FCSTD DOCUMENT  (FreeCAD 1.0R38806 (Git))
Label: ex-005
License: All rights reserved
LicenseURL: https://en.wikipedia.org/wiki/All_rights_reserved
objects: TechDraw::DrawViewDimension×18, Sketcher::SketchObject×2, TechDraw::DrawSVGTemplate×1, TechDraw::DrawProjGroupItem×1, TechDraw::DrawPage×1
note: 24 computed .brp shape members not serialized (recipe doc carries the construction recipe); baked Part::Feature solids carry a one-line shape summary decoded from their .brp

FEATURE [Sketcher::SketchObject] Sketch
  ArcFitTolerance = 1e-06
  FullyConstrained = false
  MakeInternals = false
  sketch-geometry (36):
    g0: LineSegment StartX=0 StartY=0 StartZ=0 EndX=5 EndY=0 EndZ=0
    g1: LineSegment StartX=5 StartY=0 StartZ=0 EndX=5 EndY=2 EndZ=0
    g2: LineSegment StartX=5 StartY=2 StartZ=0 EndX=3 EndY=2 EndZ=0
    g3: LineSegment StartX=3 StartY=2 StartZ=0 EndX=3 EndY=6 EndZ=0
    g4: LineSegment StartX=3 StartY=6 StartZ=0 EndX=5 EndY=6 EndZ=0
    g5: LineSegment StartX=5 StartY=6 StartZ=0 EndX=5 EndY=8 EndZ=0
    g6: LineSegment StartX=5 StartY=8 StartZ=0 EndX=9 EndY=8 EndZ=0
    g7: LineSegment StartX=9 StartY=8 StartZ=0 EndX=9 EndY=12 EndZ=0
    g8: LineSegment StartX=9 StartY=12 StartZ=0 EndX=17 EndY=12 EndZ=0
    g9: LineSegment StartX=17 StartY=12 StartZ=0 EndX=17 EndY=8 EndZ=0
    g10: LineSegment StartX=17 StartY=8 StartZ=0 EndX=21 EndY=8 EndZ=0
    g11: LineSegment StartX=21 StartY=8 StartZ=0 EndX=21 EndY=6 EndZ=0
    g12: LineSegment StartX=21 StartY=6 StartZ=0 EndX=23 EndY=6 EndZ=0
    g13: LineSegment StartX=23 StartY=6 StartZ=0 EndX=23 EndY=2 EndZ=0
    g14: LineSegment StartX=23 StartY=2 StartZ=0 EndX=21 EndY=2 EndZ=0
    g15: LineSegment StartX=21 StartY=2 StartZ=0 EndX=21 EndY=0 EndZ=0
    g16: LineSegment StartX=21 StartY=0 StartZ=0 EndX=26 EndY=0 EndZ=0
    g17: LineSegment StartX=26 StartY=0 StartZ=0 EndX=26 EndY=28 EndZ=0
    g18: LineSegment StartX=26 StartY=28 StartZ=0 EndX=21 EndY=28 EndZ=0
    g19: LineSegment StartX=21 StartY=28 StartZ=0 EndX=21 EndY=28.6161 EndZ=0
    g20: LineSegment StartX=21 StartY=28.6161 StartZ=0 EndX=20.9931 EndY=28.6161 EndZ=0
    g21: LineSegment StartX=20.9931 StartY=28.6161 StartZ=0 EndX=20.9931 EndY=26.6161 EndZ=0
    g22: LineSegment StartX=20.9931 StartY=26.6161 StartZ=0 EndX=18.9931 EndY=26.6161 EndZ=0
    g23: LineSegment StartX=18.9931 StartY=26.6161 StartZ=0 EndX=18.9931 EndY=22.6161 EndZ=0
    g24: LineSegment StartX=18.9931 StartY=22.6161 StartZ=0 EndX=14.9931 EndY=22.6161 EndZ=0
    g25: LineSegment StartX=14.9931 StartY=22.6161 StartZ=0 EndX=14.9931 EndY=18.6161 EndZ=0
    g26: LineSegment StartX=14.9931 StartY=18.6161 StartZ=0 EndX=6.99307 EndY=18.6161 EndZ=0
    g27: LineSegment StartX=6.99307 StartY=18.6161 StartZ=0 EndX=6.99307 EndY=23.0034 EndZ=0
    g28: LineSegment StartX=6.99307 StartY=23.0034 StartZ=0 EndX=6.85689 EndY=23.0034 EndZ=0
    g29: LineSegment StartX=6.85689 StartY=23.0034 StartZ=0 EndX=6.85689 EndY=24.9877 EndZ=0
    g30: LineSegment StartX=6.85689 StartY=24.9877 StartZ=0 EndX=4.95544 EndY=24.9877 EndZ=0
    g31: LineSegment StartX=4.95544 StartY=24.9877 StartZ=0 EndX=4.95544 EndY=28.9958 EndZ=0
    g32: LineSegment StartX=4.95544 StartY=28.9958 StartZ=0 EndX=7.08944 EndY=28.9958 EndZ=0
    g33: LineSegment StartX=7.08944 StartY=28.9958 StartZ=0 EndX=7.08944 EndY=30.9705 EndZ=0
    g34: LineSegment StartX=7.08944 StartY=30.9705 StartZ=0 EndX=1.97894 EndY=30.9705 EndZ=0
    g35: LineSegment StartX=1.97894 StartY=30.9705 StartZ=0 EndX=0 EndY=0 EndZ=0
  constraints (97):
    c: Coincident(g-1,g0)
    c: PointOnObject(g0,g-1)
    c: Coincident(g0,g1)
    c: Vertical(g1)
    c: Coincident(g1,g2)
    c: Horizontal(g2)
    c: Coincident(g2,g3)
    c: Vertical(g3)
    c: Coincident(g3,g4)
    c: Horizontal(g4)
    c: Coincident(g4,g5)
    c: Vertical(g5)
    c: Coincident(g5,g6)
    c: Horizontal(g6)
    c: Coincident(g6,g7)
    c: Vertical(g7)
    c: Coincident(g7,g8)
    c: Horizontal(g8)
    c: Coincident(g8,g9)
    c: Vertical(g9)
    c: Coincident(g9,g10)
    c: Horizontal(g10)
    c: Coincident(g10,g11)
    c: Vertical(g11)
    c: Coincident(g11,g12)
    c: Horizontal(g12)
    c: Coincident(g12,g13)
    c: Vertical(g13)
    c: Coincident(g13,g14)
    c: Horizontal(g14)
    c: Coincident(g14,g15)
    c: PointOnObject(g15,g-1)
    c: Vertical(g15)
    c: Coincident(g15,g16)
    c: PointOnObject(g16,g-1)
    c: Coincident(g16,g17)
    c: Vertical(g17)
    c: Coincident(g17,g18)
    c: Horizontal(g18)
    c: Coincident(g18,g19)
    c: Vertical(g19)
    c: Coincident(g19,g20)
    c: Horizontal(g20)
    c: Coincident(g20,g21)
    c: Vertical(g21)
    c: Coincident(g21,g22)
    c: Horizontal(g22)
    c: Coincident(g22,g23)
    c: Vertical(g23)
    c: Coincident(g23,g24)
    c: Horizontal(g24)
    c: Coincident(g24,g25)
    c: Vertical(g25)
    c: Coincident(g25,g26)
    c: Horizontal(g26)
    c: Coincident(g26,g27)
    c: Vertical(g27)
    c: Coincident(g27,g28)
    c: Horizontal(g28)
    c: Coincident(g28,g29)
    c: Vertical(g29)
    c: Coincident(g29,g30)
    c: Horizontal(g30)
    c: Coincident(g30,g31)
    c: Vertical(g31)
    c: Coincident(g31,g32)
    c: Horizontal(g32)
    c: Coincident(g32,g33)
    c: Vertical(g33)
    c: Coincident(g33,g34)
    c: Horizontal(g34)
    c: Coincident(g34,g35)
    c: Coincident(g35,g0)
    c: DistanceX(g0,g0) = 5
    c: DistanceY(g1,g1) = 2
    c: DistanceX(g2,g2) = 2
    c: DistanceY(g3,g3) = 4
    c: DistanceX(g4,g4) = 2
    c: DistanceY(g5,g5) = 2
    c: DistanceX(g6,g6) = 4
    c: DistanceY(g7,g7) = 4
    c: DistanceX(g8,g8) = 8
    c: DistanceY(g9,g9) = 4
    c: DistanceX(g10,g10) = 4
    c: DistanceY(g11,g11) = 2
    c: DistanceX(g12,g12) = 2
    c: DistanceY(g13,g13) = 4
    c: DistanceX(g14,g14) = 2
    c: DistanceX(g16,g16) = 5
    c: DistanceY(g17,g17) = 28
    c: DistanceX(g18,g18) = 5
    c: DistanceY(g21,g21) = 2
    c: DistanceX(g22,g22) = 2
    c: DistanceX(g24,g24) = 4
    c: DistanceY(g23,g23) = 4
    c: Distance(g25,g25) = 4
    c: DistanceX(g26,g26) = 8
FEATURE [Sketcher::SketchObject] Sketch001
  ArcFitTolerance = 1e-06
  FullyConstrained = true
  MakeInternals = false
  sketch-geometry (36):
    g0: LineSegment StartX=0 StartY=0 StartZ=0 EndX=5 EndY=0 EndZ=0
    g1: LineSegment StartX=5 StartY=0 StartZ=0 EndX=5 EndY=2 EndZ=0
    g2: LineSegment StartX=5 StartY=2 StartZ=0 EndX=3 EndY=2 EndZ=0
    g3: LineSegment StartX=3 StartY=2 StartZ=0 EndX=3 EndY=6 EndZ=0
    g4: LineSegment StartX=3 StartY=6 StartZ=0 EndX=5 EndY=6 EndZ=0
    g5: LineSegment StartX=5 StartY=6 StartZ=0 EndX=5 EndY=8 EndZ=0
    g6: LineSegment StartX=5 StartY=8 StartZ=0 EndX=9 EndY=8 EndZ=0
    g7: LineSegment StartX=9 StartY=8 StartZ=0 EndX=9 EndY=12 EndZ=0
    g8: LineSegment StartX=9 StartY=12 StartZ=0 EndX=17 EndY=12 EndZ=0
    g9: LineSegment StartX=17 StartY=12 StartZ=0 EndX=17 EndY=8 EndZ=0
    g10: LineSegment StartX=17 StartY=8 StartZ=0 EndX=21 EndY=8 EndZ=0
    g11: LineSegment StartX=21 StartY=8 StartZ=0 EndX=21 EndY=6 EndZ=0
    g12: LineSegment StartX=21 StartY=6 StartZ=0 EndX=23 EndY=6 EndZ=0
    g13: LineSegment StartX=23 StartY=6 StartZ=0 EndX=23 EndY=2 EndZ=0
    g14: LineSegment StartX=23 StartY=2 StartZ=0 EndX=21 EndY=2 EndZ=0
    g15: LineSegment StartX=21 StartY=2 StartZ=0 EndX=21 EndY=0 EndZ=0
    g16: LineSegment StartX=21 StartY=0 StartZ=0 EndX=26 EndY=0 EndZ=0
    g17: LineSegment StartX=26 StartY=0 StartZ=0 EndX=26 EndY=28 EndZ=0
    g18: LineSegment StartX=26 StartY=28 StartZ=0 EndX=21 EndY=28 EndZ=0
    g19: LineSegment StartX=21 StartY=28 StartZ=0 EndX=21 EndY=26 EndZ=0
    g20: LineSegment StartX=21 StartY=26 StartZ=0 EndX=23 EndY=26 EndZ=0
    g21: LineSegment StartX=23 StartY=26 StartZ=0 EndX=23 EndY=22 EndZ=0
    g22: LineSegment StartX=23 StartY=22 StartZ=0 EndX=21 EndY=22 EndZ=0
    g23: LineSegment StartX=21 StartY=22 StartZ=0 EndX=21 EndY=20 EndZ=0
    g24: LineSegment StartX=21 StartY=20 StartZ=0 EndX=17 EndY=20 EndZ=0
    g25: LineSegment StartX=17 StartY=20 StartZ=0 EndX=17 EndY=16 EndZ=0
    g26: LineSegment StartX=17 StartY=16 StartZ=0 EndX=9 EndY=16 EndZ=0
    g27: LineSegment StartX=9 StartY=16 StartZ=0 EndX=9 EndY=20 EndZ=0
    g28: LineSegment StartX=9 StartY=20 StartZ=0 EndX=5 EndY=20 EndZ=0
    g29: LineSegment StartX=5 StartY=20 StartZ=0 EndX=5 EndY=22 EndZ=0
    g30: LineSegment StartX=5 StartY=22 StartZ=0 EndX=3 EndY=22 EndZ=0
    g31: LineSegment StartX=3 StartY=22 StartZ=0 EndX=3 EndY=26 EndZ=0
    g32: LineSegment StartX=3 StartY=26 StartZ=0 EndX=5 EndY=26 EndZ=0
    g33: LineSegment StartX=5 StartY=26 StartZ=0 EndX=5 EndY=28 EndZ=0
    g34: LineSegment StartX=5 StartY=28 StartZ=0 EndX=0 EndY=28 EndZ=0
    g35: LineSegment StartX=0 StartY=28 StartZ=0 EndX=0 EndY=0 EndZ=0
  constraints (107):
    c: Coincident(g-1,g0)
    c: PointOnObject(g0,g-1)
    c: Coincident(g0,g1)
    c: Vertical(g1)
    c: Coincident(g1,g2)
    c: Horizontal(g2)
    c: Coincident(g2,g3)
    c: Vertical(g3)
    c: Coincident(g3,g4)
    c: Horizontal(g4)
    c: Coincident(g4,g5)
    c: Vertical(g5)
    c: Coincident(g5,g6)
    c: Horizontal(g6)
    c: Coincident(g6,g7)
    c: Vertical(g7)
    c: Coincident(g7,g8)
    c: Horizontal(g8)
    c: Coincident(g8,g9)
    c: Vertical(g9)
    c: Coincident(g9,g10)
    c: Horizontal(g10)
    c: Coincident(g10,g11)
    c: Vertical(g11)
    c: Coincident(g11,g12)
    c: Horizontal(g12)
    c: Coincident(g12,g13)
    c: Vertical(g13)
    c: Coincident(g13,g14)
    c: Horizontal(g14)
    c: Coincident(g14,g15)
    c: PointOnObject(g15,g-1)
    c: Coincident(g15,g16)
    c: PointOnObject(g16,g-1)
    c: Coincident(g16,g17)
    c: Vertical(g17)
    c: Coincident(g17,g18)
    c: Horizontal(g18)
    c: Coincident(g18,g19)
    c: Vertical(g19)
    c: Coincident(g19,g20)
    c: Coincident(g20,g21)
    c: Vertical(g21)
    c: Coincident(g21,g22)
    c: Horizontal(g22)
    c: Coincident(g22,g23)
    c: Vertical(g23)
    c: Coincident(g23,g24)
    c: Horizontal(g24)
    c: Coincident(g24,g25)
    c: Vertical(g25)
    c: Coincident(g25,g26)
    c: Horizontal(g26)
    c: Coincident(g26,g27)
    c: Vertical(g27)
    c: Coincident(g27,g28)
    c: Horizontal(g28)
    c: Coincident(g28,g29)
    c: Vertical(g29)
    c: Coincident(g29,g30)
    c: Horizontal(g30)
    c: Coincident(g30,g31)
    c: Vertical(g31)
    c: Coincident(g31,g32)
    c: Horizontal(g32)
    c: Coincident(g32,g33)
    c: Vertical(g33)
    c: Coincident(g33,g34)
    c: Horizontal(g34)
    c: Coincident(g34,g35)
    c: Coincident(g35,g0)
    c: Vertical(g35)
    c: DistanceX(g0,g0) = 5
    c: DistanceY(g1,g1) = 2
    c: DistanceX(g2,g2) = 2
    c: DistanceY(g3,g3) = 4
    c: DistanceX(g4,g4) = 2
    c: DistanceY(g5,g5) = 2
    c: DistanceX(g6,g6) = 4
    c: DistanceY(g7,g7) = 4
    c: DistanceX(g8,g8) = 8
    c: DistanceY(g9,g9) = 4
    c: DistanceX(g10,g10) = 4
    c: DistanceY(g11,g11) = 2
    c: DistanceX(g12,g12) = 2
    c: DistanceY(g13,g13) = 4
    c: DistanceX(g14,g14) = 2
    c: DistanceX(g16,g16) = 5
    c: DistanceY(g17,g17) = 28
    c: DistanceX(g18,g18) = 5
    c: DistanceY(g19,g19) = 2
    c: DistanceX(g20,g20) = 2
    c: DistanceY(g21,g21) = 4
    c: DistanceX(g22,g22) = 2
    c: DistanceY(g23,g23) = 2
    c: DistanceX(g24,g24) = 4
    c: DistanceY(g25,g25) = 4
    c: DistanceX(g26,g26) = 8
    c: DistanceY(g27,g27) = 4
    c: DistanceX(g28,g28) = 4
    c: Distance(g29,g29) = 2
    c: DistanceX(g30,g30) = 2
    c: DistanceY(g31,g31) = 4
    c: DistanceX(g32,g32) = 2
    c: DistanceY(g33,g33) = 2
    c: DistanceX(g34,g34) = 5
    c: DistanceY(g35,g35) = 28
FEATURE [TechDraw::DrawSVGTemplate] Template
  EditableTexts = Numero de ejercicio=000
  Height = 297
  Orientation = 0
  Template = <userpath>/Downloads/Freecad-Mechanical-A4.svg
  Width = 210
FEATURE [TechDraw::DrawProjGroupItem] View
  CoarseView = false
  Direction = (0,0,1)
  Focus = 100
  HardHidden = false
  IsoCount = 0
  IsoHidden = false
  IsoVisible = false
  LockPosition = false
  Perspective = false
  Rotation = 0
  RotationVector = (1,0,0)
  Scale = 5
  ScaleType = 0
  ScrubCount = 1
  SeamHidden = false
  SeamVisible = false
  SmoothHidden = false
  SmoothVisible = true
  Source = -> [Sketch001]
  Type = 0
  X = 105.21
  XDirection = (1,0,0)
  Y = 184.053
FEATURE [TechDraw::DrawViewDimension] Dimension
  AngleOverride = false
  Arbitrary = false
  ArbitraryTolerances = false
  BoxCorners = (2) [(-65,-70,0),(65,70,0)]
  EqualTolerance = true
  ExtensionAngle = 0
  FormatSpec = %.2w
  FormatSpecOverTolerance = %+.2w
  FormatSpecUnderTolerance = %+.2w
  Inverted = false
  LineAngle = 0
  LockPosition = false
  MeasureType = 1
  OverTolerance = 0
  References2D = -> [View]
  Rotation = 0
  Scale = 5
  ScaleType = 0
  TheoreticalExact = false
  Type = 1
  UnderTolerance = 0
  X = -52.5
  Y = -97.3097
FEATURE [TechDraw::DrawViewDimension] Dimension001
  AngleOverride = false
  Arbitrary = false
  ArbitraryTolerances = false
  BoxCorners = (2) [(-65,-70,0),(65,70,0)]
  EqualTolerance = true
  ExtensionAngle = 0
  FormatSpec = %.2w
  FormatSpecOverTolerance = %+.2w
  FormatSpecUnderTolerance = %+.2w
  Inverted = false
  LineAngle = 0
  LockPosition = false
  MeasureType = 1
  OverTolerance = 0
  References2D = -> [View]
  Rotation = 0
  Scale = 5
  ScaleType = 0
  TheoreticalExact = false
  Type = 1
  UnderTolerance = 0
  X = -30
  Y = -97.3097
FEATURE [TechDraw::DrawViewDimension] Dimension002
  AngleOverride = false
  Arbitrary = false
  ArbitraryTolerances = false
  BoxCorners = (2) [(-65,-70,0),(65,70,0)]
  EqualTolerance = true
  ExtensionAngle = 0
  FormatSpec = %.2w
  FormatSpecOverTolerance = %+.2w
  FormatSpecUnderTolerance = %+.2w
  Inverted = false
  LineAngle = 0
  LockPosition = false
  MeasureType = 1
  OverTolerance = 0
  References2D = -> [View]
  Rotation = 0
  Scale = 5
  ScaleType = 0
  TheoreticalExact = false
  Type = 1
  UnderTolerance = 0
  X = 0
  Y = -97.3097
FEATURE [TechDraw::DrawViewDimension] Dimension003
  AngleOverride = false
  Arbitrary = false
  ArbitraryTolerances = false
  BoxCorners = (2) [(-65,-70,0),(65,70,0)]
  EqualTolerance = true
  ExtensionAngle = 0
  FormatSpec = %.2w
  FormatSpecOverTolerance = %+.2w
  FormatSpecUnderTolerance = %+.2w
  Inverted = false
  LineAngle = 0
  LockPosition = false
  MeasureType = 1
  OverTolerance = 0
  References2D = -> [View]
  Rotation = 0
  Scale = 5
  ScaleType = 0
  TheoreticalExact = false
  Type = 1
  UnderTolerance = 0
  X = 32.8593
  Y = -97.3097
FEATURE [TechDraw::DrawViewDimension] Dimension004
  AngleOverride = false
  Arbitrary = false
  ArbitraryTolerances = false
  BoxCorners = (2) [(-65,-70,0),(65,70,0)]
  EqualTolerance = true
  ExtensionAngle = 0
  FormatSpec = %.2w
  FormatSpecOverTolerance = %+.2w
  FormatSpecUnderTolerance = %+.2w
  Inverted = false
  LineAngle = 0
  LockPosition = false
  MeasureType = 1
  OverTolerance = 0
  References2D = -> [View]
  Rotation = 0
  Scale = 5
  ScaleType = 0
  TheoreticalExact = false
  Type = 1
  UnderTolerance = 0
  X = 52.5
  Y = -97.3097
FEATURE [TechDraw::DrawViewDimension] Dimension008
  AngleOverride = false
  Arbitrary = false
  ArbitraryTolerances = false
  BoxCorners = (2) [(-65,-70,0),(65,70,0)]
  EqualTolerance = true
  ExtensionAngle = 0
  FormatSpec = %.2w
  FormatSpecOverTolerance = %+.2w
  FormatSpecUnderTolerance = %+.2w
  Inverted = false
  LineAngle = 0
  LockPosition = false
  MeasureType = 1
  OverTolerance = 0
  References2D = -> [View]
  Rotation = 0
  Scale = 5
  ScaleType = 0
  TheoreticalExact = false
  Type = 2
  UnderTolerance = 0
  X = -77.2737
  Y = 7.90733
FEATURE [TechDraw::DrawViewDimension] Dimension009
  AngleOverride = false
  Arbitrary = false
  ArbitraryTolerances = false
  BoxCorners = (2) [(-65,-70,0),(65,70,0)]
  EqualTolerance = true
  ExtensionAngle = 0
  FormatSpec = %.2w
  FormatSpecOverTolerance = %+.2w
  FormatSpecUnderTolerance = %+.2w
  Inverted = false
  LineAngle = 0
  LockPosition = false
  MeasureType = 1
  OverTolerance = 0
  References2D = -> [View]
  Rotation = 0
  Scale = 5
  ScaleType = 0
  TheoreticalExact = false
  Type = 0
  UnderTolerance = 0
  X = 80.4211
  Y = -65
FEATURE [TechDraw::DrawViewDimension] Dimension010
  AngleOverride = false
  Arbitrary = false
  ArbitraryTolerances = false
  BoxCorners = (2) [(-65,-70,0),(65,70,0)]
  EqualTolerance = true
  ExtensionAngle = 0
  FormatSpec = %.2w
  FormatSpecOverTolerance = %+.2w
  FormatSpecUnderTolerance = %+.2w
  Inverted = false
  LineAngle = 0
  LockPosition = false
  MeasureType = 1
  OverTolerance = 0
  References2D = -> [View]
  Rotation = 0
  Scale = 5
  ScaleType = 0
  TheoreticalExact = false
  Type = 2
  UnderTolerance = 0
  X = 80.4211
  Y = -50
FEATURE [TechDraw::DrawViewDimension] Dimension011
  AngleOverride = false
  Arbitrary = false
  ArbitraryTolerances = false
  BoxCorners = (2) [(-65,-70,0),(65,70,0)]
  EqualTolerance = true
  ExtensionAngle = 0
  FormatSpec = %.2w
  FormatSpecOverTolerance = %+.2w
  FormatSpecUnderTolerance = %+.2w
  Inverted = false
  LineAngle = 0
  LockPosition = false
  MeasureType = 1
  OverTolerance = 0
  References2D = -> [View]
  Rotation = 0
  Scale = 5
  ScaleType = 0
  TheoreticalExact = false
  Type = 0
  UnderTolerance = 0
  X = 80.4211
  Y = -35
FEATURE [TechDraw::DrawViewDimension] Dimension012
  AngleOverride = false
  Arbitrary = false
  ArbitraryTolerances = false
  BoxCorners = (2) [(-65,-70,0),(65,70,0)]
  EqualTolerance = true
  ExtensionAngle = 0
  FormatSpec = %.2w
  FormatSpecOverTolerance = %+.2w
  FormatSpecUnderTolerance = %+.2w
  Inverted = false
  LineAngle = 0
  LockPosition = false
  MeasureType = 1
  OverTolerance = 0
  References2D = -> [View]
  Rotation = 0
  Scale = 5
  ScaleType = 0
  TheoreticalExact = false
  Type = 2
  UnderTolerance = 0
  X = 80.4211
  Y = -20
FEATURE [TechDraw::DrawViewDimension] Dimension013
  AngleOverride = false
  Arbitrary = false
  ArbitraryTolerances = false
  BoxCorners = (2) [(-65,-70,0),(65,70,0)]
  EqualTolerance = true
  ExtensionAngle = 0
  FormatSpec = %.2w
  FormatSpecOverTolerance = %+.2w
  FormatSpecUnderTolerance = %+.2w
  Inverted = false
  LineAngle = 0
  LockPosition = false
  MeasureType = 1
  OverTolerance = 0
  References2D = -> [View]
  Rotation = 0
  Scale = 5
  ScaleType = 0
  TheoreticalExact = false
  Type = 2
  UnderTolerance = 0
  X = 80.4211
  Y = 0
FEATURE [TechDraw::DrawViewDimension] Dimension014
  AngleOverride = false
  Arbitrary = false
  ArbitraryTolerances = false
  BoxCorners = (2) [(-65,-70,0),(65,70,0)]
  EqualTolerance = true
  ExtensionAngle = 0
  FormatSpec = %.2w
  FormatSpecOverTolerance = %+.2w
  FormatSpecUnderTolerance = %+.2w
  Inverted = false
  LineAngle = 0
  LockPosition = false
  MeasureType = 1
  OverTolerance = 0
  References2D = -> [View]
  Rotation = 0
  Scale = 5
  ScaleType = 0
  TheoreticalExact = false
  Type = 2
  UnderTolerance = 0
  X = 80.4211
  Y = 20
FEATURE [TechDraw::DrawViewDimension] Dimension015
  AngleOverride = false
  Arbitrary = false
  ArbitraryTolerances = false
  BoxCorners = (2) [(-65,-70,0),(65,70,0)]
  EqualTolerance = true
  ExtensionAngle = 0
  FormatSpec = %.2w
  FormatSpecOverTolerance = %+.2w
  FormatSpecUnderTolerance = %+.2w
  Inverted = false
  LineAngle = 0
  LockPosition = false
  MeasureType = 1
  OverTolerance = 0
  References2D = -> [View]
  Rotation = 0
  Scale = 5
  ScaleType = 0
  TheoreticalExact = false
  Type = 2
  UnderTolerance = 0
  X = 80.4211
  Y = 35
FEATURE [TechDraw::DrawViewDimension] Dimension016
  AngleOverride = false
  Arbitrary = false
  ArbitraryTolerances = false
  BoxCorners = (2) [(-65,-70,0),(65,70,0)]
  EqualTolerance = true
  ExtensionAngle = 0
  FormatSpec = %.2w
  FormatSpecOverTolerance = %+.2w
  FormatSpecUnderTolerance = %+.2w
  Inverted = false
  LineAngle = 0
  LockPosition = false
  MeasureType = 1
  OverTolerance = 0
  References2D = -> [View]
  Rotation = 0
  Scale = 5
  ScaleType = 0
  TheoreticalExact = false
  Type = 2
  UnderTolerance = 0
  X = 80.4211
  Y = 50
FEATURE [TechDraw::DrawViewDimension] Dimension017
  AngleOverride = false
  Arbitrary = false
  ArbitraryTolerances = false
  BoxCorners = (2) [(-65,-70,0),(65,70,0)]
  EqualTolerance = true
  ExtensionAngle = 0
  FormatSpec = %.2w
  FormatSpecOverTolerance = %+.2w
  FormatSpecUnderTolerance = %+.2w
  Inverted = false
  LineAngle = 0
  LockPosition = false
  MeasureType = 1
  OverTolerance = 0
  References2D = -> [View]
  Rotation = 0
  Scale = 5
  ScaleType = 0
  TheoreticalExact = false
  Type = 0
  UnderTolerance = 0
  X = 80.4211
  Y = 65
FEATURE [TechDraw::DrawViewDimension] Dimension018
  AngleOverride = false
  Arbitrary = false
  ArbitraryTolerances = false
  BoxCorners = (2) [(-65,-70,0),(65,70,0)]
  EqualTolerance = true
  ExtensionAngle = 0
  FormatSpec = %.2w
  FormatSpecOverTolerance = %+.2w
  FormatSpecUnderTolerance = %+.2w
  Inverted = false
  LineAngle = 0
  LockPosition = false
  MeasureType = 1
  OverTolerance = 0
  References2D = -> [View]
  Rotation = 0
  Scale = 5
  ScaleType = 0
  TheoreticalExact = false
  Type = 1
  UnderTolerance = 0
  X = 45
  Y = -45.6521
FEATURE [TechDraw::DrawViewDimension] Dimension019
  AngleOverride = false
  Arbitrary = false
  ArbitraryTolerances = false
  BoxCorners = (2) [(-65,-70,0),(65,70,0)]
  EqualTolerance = true
  ExtensionAngle = 0
  FormatSpec = %.2w
  FormatSpecOverTolerance = %+.2w
  FormatSpecUnderTolerance = %+.2w
  Inverted = false
  LineAngle = 0
  LockPosition = false
  MeasureType = 1
  OverTolerance = 0
  References2D = -> [View]
  Rotation = 0
  Scale = 5
  ScaleType = 0
  TheoreticalExact = false
  Type = 1
  UnderTolerance = 0
  X = -45
  Y = -47.6159
FEATURE [TechDraw::DrawViewDimension] Dimension020
  AngleOverride = false
  Arbitrary = false
  ArbitraryTolerances = false
  BoxCorners = (2) [(-65,-70,0),(65,70,0)]
  EqualTolerance = true
  ExtensionAngle = 0
  FormatSpec = %.2w
  FormatSpecOverTolerance = %+.2w
  FormatSpecUnderTolerance = %+.2w
  Inverted = false
  LineAngle = 0
  LockPosition = false
  MeasureType = 1
  OverTolerance = 0
  References2D = -> [View]
  Rotation = 0
  Scale = 5
  ScaleType = 0
  TheoreticalExact = false
  Type = 1
  UnderTolerance = 0
  X = -2.82962
  Y = -111.112
FEATURE [TechDraw::DrawPage] Page
  KeepUpdated = true
  NextBalloonIndex = 1
  ProjectionType = 0
  Scale = 5
  Template = -> Template
  Views = -> [View,Dimension,Dimension001,Dimension002,Dimension003,Dimension004,Dimension008,Dimension009,Dimension010,Dimension011,Dimension012,Dimension013,Dimension014,Dimension015,Dimension016,Dimension017,Dimension018,Dimension019,Dimension020]
